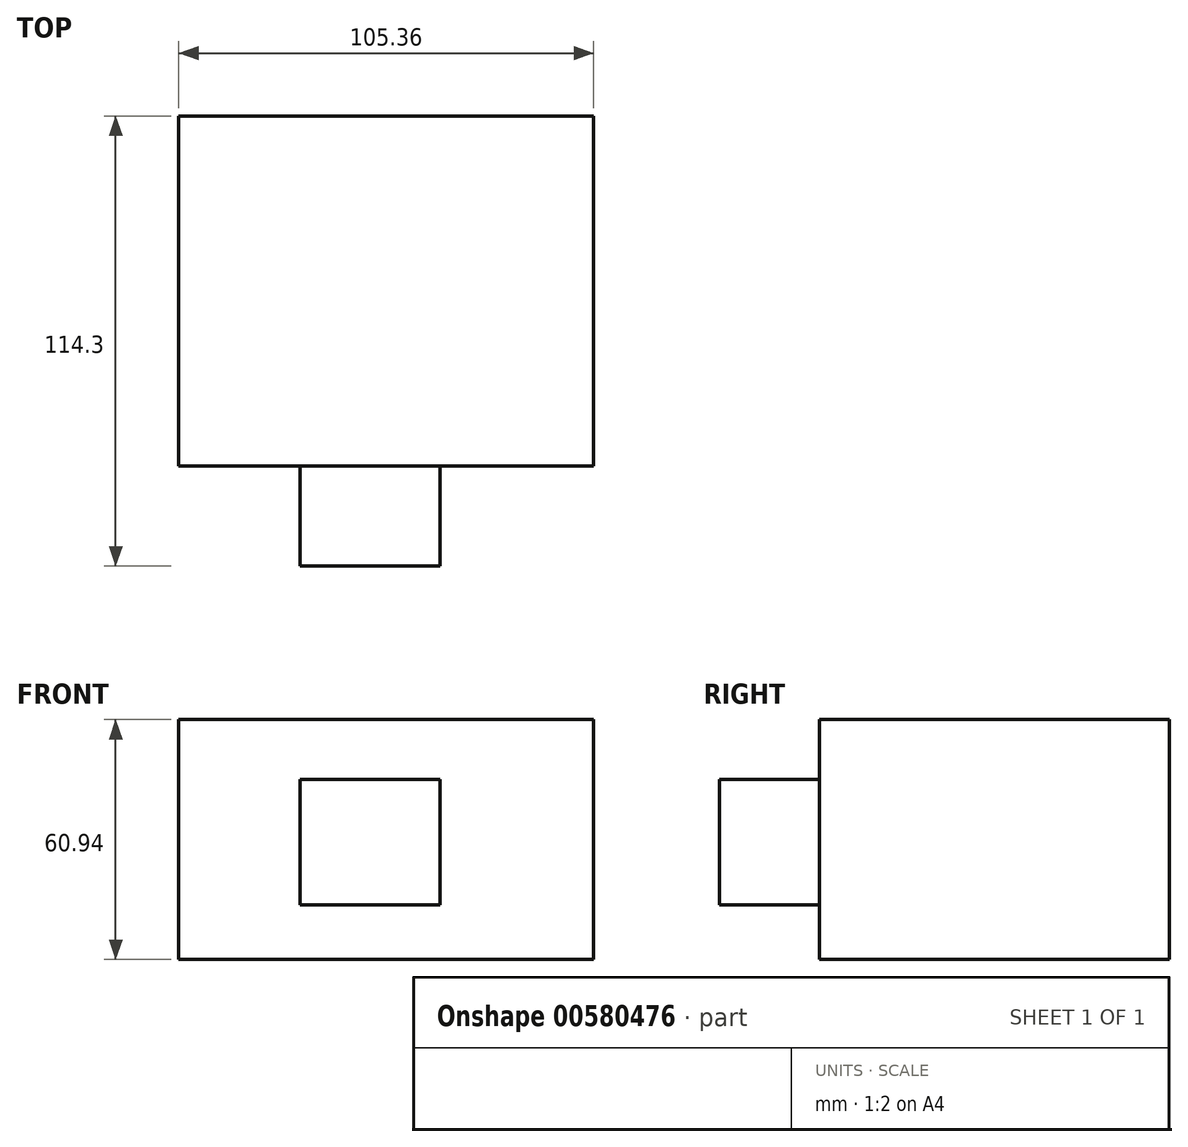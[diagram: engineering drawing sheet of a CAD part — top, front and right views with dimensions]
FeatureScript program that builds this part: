
annotation { "Feature Type Name" : "Feature", "Feature Type Description" : "" }
export const myFeature = defineFeature(function(context is Context, id is Id, definition is map)
    precondition{}
    {
        {
            var Q0;
            Q0=qCreatedBy(makeId("Front.planeOp"),FACE);
            var sketch = newSketch(context, id + "F0", { "sketchPlane" : qUnion([Q0])});
            skLineSegment(sketch, "E0.bottom", {"start": v(-48.61, 31.17) * mm, "end": v(56.75, 31.17) * mm});
            skLineSegment(sketch, "E0.top", {"start": v(-48.61, -29.77) * mm, "end": v(56.75, -29.77) * mm});
            skLineSegment(sketch, "E0.left", {"start": v(-48.61, 31.17) * mm, "end": v(-48.61, -29.77) * mm});
            skLineSegment(sketch, "E0.right", {"start": v(56.75, 31.17) * mm, "end": v(56.75, -29.77) * mm});
            skSolve(sketch);
        }
        {
            var Q0;
            Q0=makeQuery(id+"F0.imprint","IMPRINT",FACE,{"disambiguationData":[TD([[makeQuery(id+"F0.imprint","IMPRINT",EDGE,{"derivedFrom":sQuery(id+"F0.wireOp",EDGE,"E0.bottom")}),-1.0]])]});
            extrude(context, id + "F1", {"entities" : qUnion([Q0]), "depth" : 88.9 * mm, "offsetDistance" : 25.4 * mm});
        }
        {
            var Q0;
            Q0=makeQuery(id+"F1.opExtrude","CAP_FACE",FACE,{"disambiguationData":[OSD([sQuery(id+"F0.wireOp",EDGE,"E0.bottom"),sQuery(id+"F0.wireOp",EDGE,"E0.top"),sQuery(id+"F0.wireOp",EDGE,"E0.left"),sQuery(id+"F0.wireOp",EDGE,"E0.right")])],"isStart":false});
            var sketch = newSketch(context, id + "F2", { "sketchPlane" : qUnion([Q0])});
            skLineSegment(sketch, "E1.bottom", {"start": v(-17.8, -15.93) * mm, "end": v(17.8, -15.93) * mm});
            skLineSegment(sketch, "E1.top", {"start": v(-17.8, 15.93) * mm, "end": v(17.8, 15.93) * mm});
            skLineSegment(sketch, "E1.left", {"start": v(-17.8, -15.93) * mm, "end": v(-17.8, 15.93) * mm});
            skLineSegment(sketch, "E1.right", {"start": v(17.8, -15.93) * mm, "end": v(17.8, 15.93) * mm});
            skPoint(sketch, "E1.middle", {"position": v(0, 0) * mm});
            skSolve(sketch);
        }
        {
            var Q0;
            Q0=makeQuery(id+"F2.imprint","IMPRINT",FACE,{"disambiguationData":[TD([[makeQuery(id+"F2.imprint","IMPRINT",EDGE,{"derivedFrom":sQuery(id+"F2.wireOp",EDGE,"E1.bottom")}),1.0]])]});
            extrude(context, id + "F3", {"entities" : qUnion([Q0]), "operationType" : NewBodyOperationType.ADD, "depth" : 25.4 * mm, "offsetDistance" : 25.4 * mm});
        }
    });
